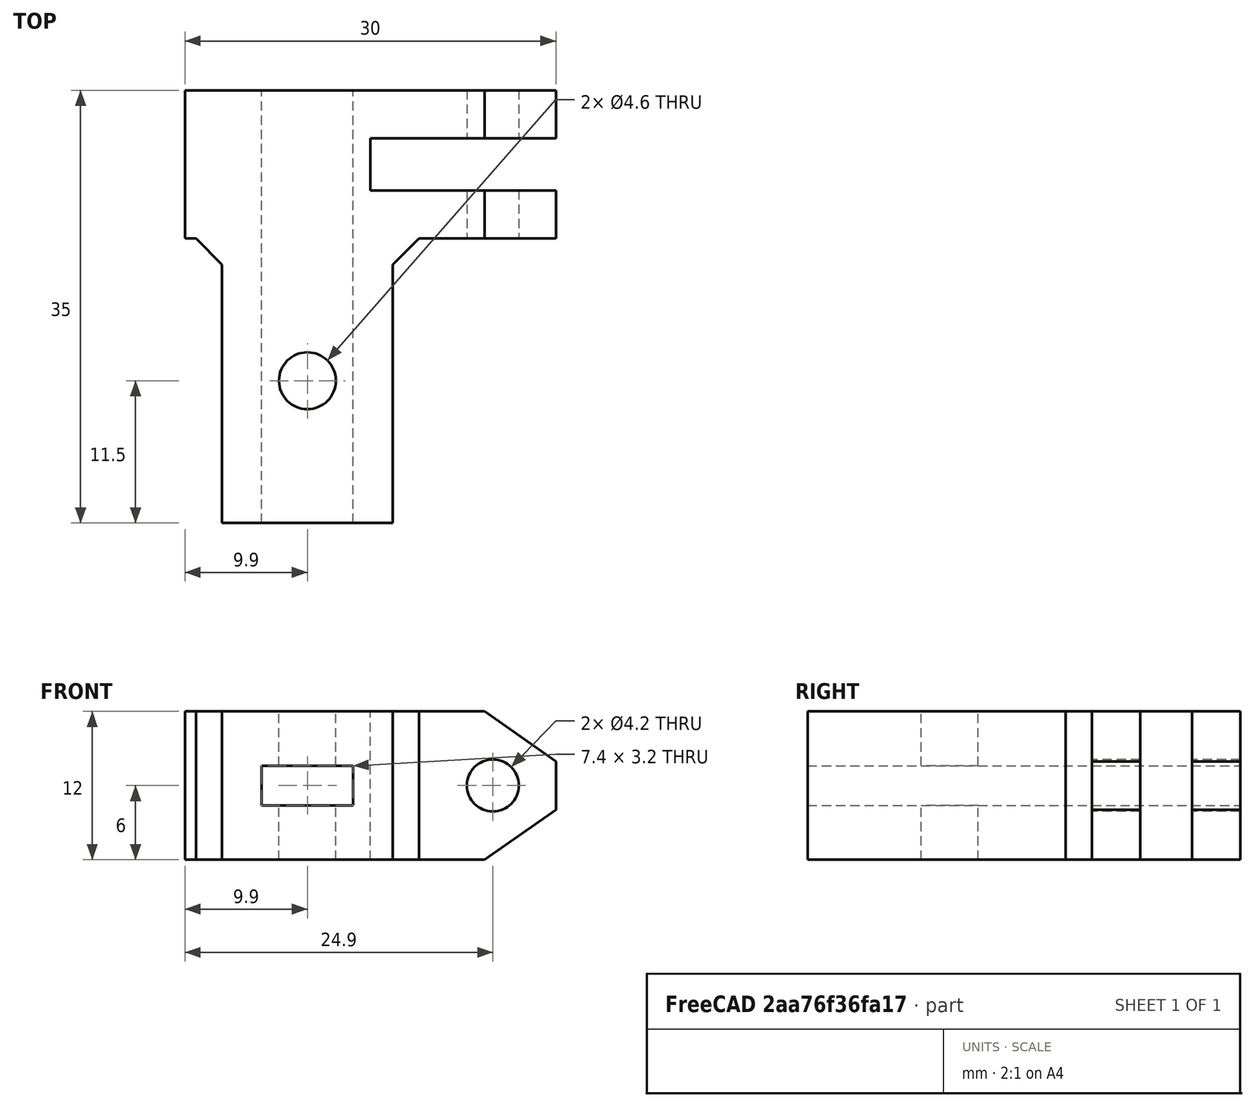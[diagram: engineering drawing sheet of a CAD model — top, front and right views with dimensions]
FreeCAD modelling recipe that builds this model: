
FCSTD DOCUMENT  (FreeCAD 0.19R23634 (Git))
Label: Stage-UpDown
License: All rights reserved
LicenseURL: http://en.wikipedia.org/wiki/All_rights_reserved
objects: Part::Prism×4, Part::Box×4, Part::Cylinder×2, Part::MultiFuse×2, Part::Cut×1, PartDesign::FeatureBase×1, PartDesign::CoordinateSystem×1, PartDesign::Body×1, App::Part×1
note: 16 computed .brp shape members not serialized (recipe doc carries the construction recipe); baked Part::Feature solids carry a one-line shape summary decoded from their .brp

FEATURE [Part::Prism] prism016
  AttacherType = Attacher::AttachEngine3D
  Circumradius = 5.25
  FirstAngle = 0
  Height = 13
  Placement = pos=(18.9,64,72) rot=(0.742942,0.473306,-0.473306;1.86366rad)
  Polygon = 3
  SecondAngle = 0
FEATURE [Part::Box] cube020
  AttacherType = Attacher::AttachEngine3D
  Height = 12
  Length = 13.8
  Placement = pos=(-6.9,28.5,60) rot=(0,0,1;0rad)
  Width = 23
FEATURE [Part::Box] cube022
  AttacherType = Attacher::AttachEngine3D
  Height = 3.2
  Length = 7.4
  Placement = pos=(-3.7,15,64.4) rot=(0,0,1;0rad)
  Width = 50
FEATURE [Part::Cylinder] cylinder014
  Angle = 360
  AttacherType = Attacher::AttachEngine3D
  Height = 13
  Placement = pos=(15,64,66) rot=(1,0,0;1.5708rad)
  Radius = 2.1
FEATURE [Part::Box] cube023
  AttacherType = Attacher::AttachEngine3D
  Height = 12
  Length = 15
  Placement = pos=(5.1,55.4,60) rot=(0,0,1;0rad)
  Width = 4.2
FEATURE [Part::Box] cube021
  AttacherType = Attacher::AttachEngine3D
  Height = 12
  Length = 30
  Placement = pos=(-9.9,51.5,60) rot=(0,0,1;0rad)
  Width = 12
FEATURE [Part::Prism] prism017
  AttacherType = Attacher::AttachEngine3D
  Circumradius = 5.25
  FirstAngle = 0
  Height = 13
  Placement = pos=(18.9,64,60) rot=(0.030858,0.70677,-0.70677;3.0799rad)
  Polygon = 3
  SecondAngle = 0
FEATURE [Part::Prism] prism015
  AttacherType = Attacher::AttachEngine3D
  Circumradius = 3
  FirstAngle = 0
  Height = 12
  Placement = pos=(-7,51.6,60) rot=(0,0,-1;1.309rad)
  Polygon = 3
  SecondAngle = 0
FEATURE [Part::Prism] prism014
  AttacherType = Attacher::AttachEngine3D
  Circumradius = 3
  FirstAngle = 0
  Height = 12
  Placement = pos=(7,51.6,60) rot=(0,0,1;0.261799rad)
  Polygon = 3
  SecondAngle = 0
FEATURE [Part::MultiFuse] Group008
  Shapes = -> [cube020,prism014,prism015,cube021]
FEATURE [Part::Cylinder] cylinder013
  Angle = 360
  AttacherType = Attacher::AttachEngine3D
  Height = 41
  Placement = pos=(0,40,51.5) rot=(0,0,1;0rad)
  Radius = 2.3
FEATURE [Part::MultiFuse] Group009
  Shapes = -> [cylinder013,cube022,cube023,cylinder014,prism016,prism017]
FEATURE [Part::Cut] difference005
  Base = -> Group008
  Tool = -> Group009
FEATURE [PartDesign::FeatureBase] BaseFeature005
  BaseFeature = -> difference005
FEATURE [PartDesign::CoordinateSystem] LCS_0
  AttacherType = Attacher::AttachEngine3D
  MapMode = 45
  Placement = pos=(-4e-16,39.8093,60) rot=(0,0,1;0rad)
  Support = -> [BaseFeature005]
FEATURE [PartDesign::Body] Body005  label="UpDown001"
  BaseFeature = -> difference005
  Group = -> [BaseFeature005]
  Origin = -> Origin005
  Tip = -> BaseFeature005
FEATURE [App::Part] UpDown
  Group = -> [LCS_0,cube021,cube020,prism016,cube023,prism017,cube022,cylinder014,Group008,Group009,prism015,prism014,difference005,cylinder013,Body005]
  Origin = -> Origin
